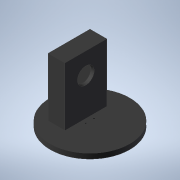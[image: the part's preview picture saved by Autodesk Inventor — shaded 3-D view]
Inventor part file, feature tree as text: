
AUTODESK INVENTOR PART (.ipt)
format: ipt  version: 2022 (Build 260153000, 153)  size: 200,704 bytes
history: native  units: in
note: dims shown in document units (in); Inventor stores cm internally (conversion verified against a paired STEP export)
features: sketch x8, extrude x7, thread x4
ambient origin geometry x8: Origin, YZ Plane, XZ Plane, XY Plane, X Axis, Y Axis, Z Axis, Center Point
bodies: Solid1 (feature_tree)
feature tree (19):
  extrude  "Extrusion1"  Depth=0.2362in TaperAngle=0.0deg
  extrude  "Extrusion2"  Depth=0.7874in
  sketch  "Sketch3"  dims[d5=0.0787in d6=0.9237in d7=0.0in]
  extrude  "Extrusion3"  Depth=0.9237in TaperAngle=0.0deg
  extrude  "Extrusion4"  Depth=0.3937in
  extrude  "Extrusion5"  Depth=1.9685in
  extrude  "Extrusion6"  Depth=2.7559in TaperAngle=0.0deg
  thread  "Thread1"  [1 undecoded]
  thread  "Thread2"  [1 undecoded]
  thread  "Thread3"  [1 undecoded]
  thread  "Thread4"  [1 undecoded]
  extrude  "Extrusion7"  Depth=0.6299in TaperAngle=0.0deg
  sketch  "Sketch1"  dims[d0=3.7402in d1=0.2362in d2=0.0in]
  sketch  "Sketch2"  dims[d3=0.7874in d4=0.0787in]
  sketch  "Sketch4"  dims[d9=0.3937in d10=0.9843in]
  sketch  "Sketch5"  dims[d11=0.5906in d12=1.9685in]
  sketch  "Sketch6"  dims[d13=0.7874in d14=2.7559in d15=0.0in d16=0.3937in d17=0.7874in d18=0.7874in d19=0.7874in]
  sketch  "Sketch7"  dims[d20=1.5945in d21=0.6299in d22=0.0in]
  sketch  "Sketch8"  dims[d23=0.2362in d24=0.2362in d25=0.2362in d26=0.0in d27=0.1024in d28=0.1181in d29=0.1181in d30=0.1969in d31=0.1969in d32=0.1063in d33=0.1063in d34=0.1063in d35=0.1063in d36=0.3937in d37=0.0in d38=0.3937in d39=0.0in d40=0.3937in d41=0.0in d42=0.3937in d43=0.0in d44=0.3937in d45=0.0in d46=0.6693in d47=0.7874in d48=0.6063in d49=0.0in]
note: 4 required parameter values undecoded (feature->parameter linkage not recoverable at this tier; creation-order binding heuristic only, values carry confidence <= 0.55)
